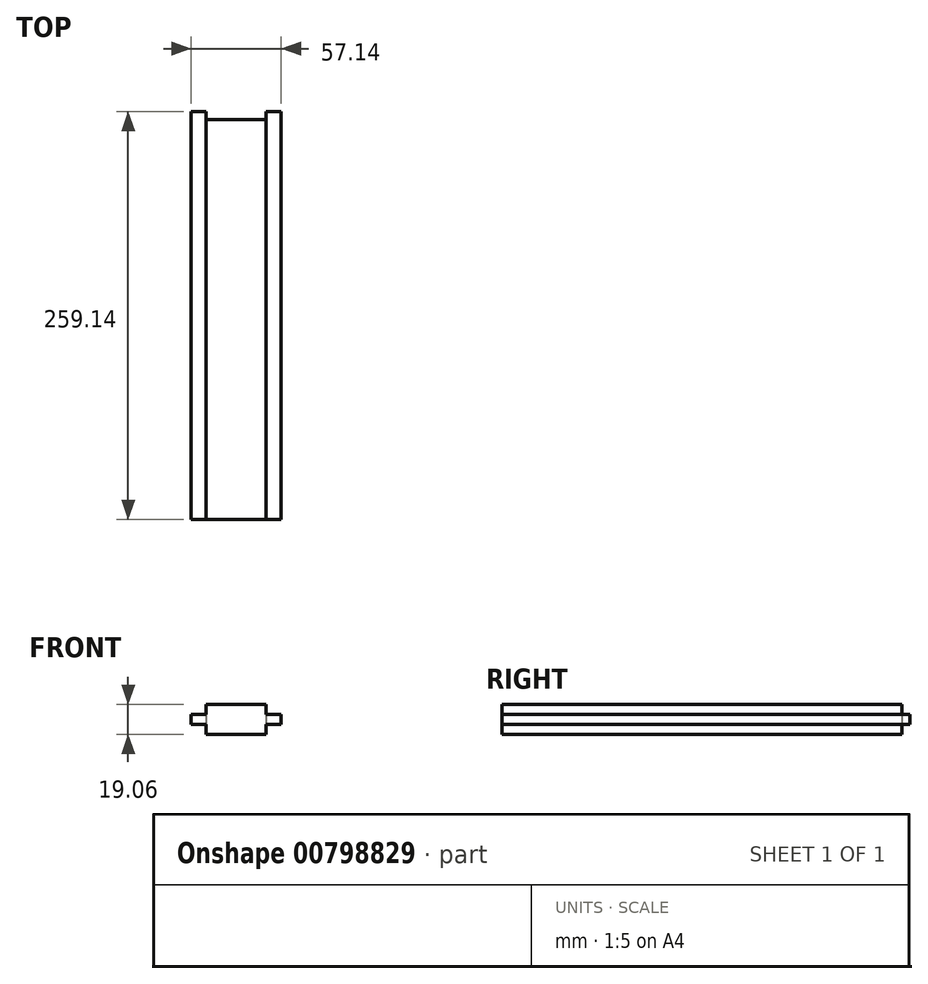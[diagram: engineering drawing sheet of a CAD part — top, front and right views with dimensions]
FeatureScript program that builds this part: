
annotation { "Feature Type Name" : "Feature", "Feature Type Description" : "" }
export const myFeature = defineFeature(function(context is Context, id is Id, definition is map)
    precondition{}
    {
        {
            var Q0;
            Q0=qCreatedBy(makeId("Front.planeOp"),FACE);
            var sketch = newSketch(context, id + "F0", { "sketchPlane" : qUnion([Q0])});
            skLineSegment(sketch, "E0.bottom", {"start": v(-19.05, 9.52) * mm, "end": v(19.05, 9.52) * mm});
            skLineSegment(sketch, "E0.top", {"start": v(-19.05, -9.53) * mm, "end": v(19.05, -9.53) * mm});
            skLineSegment(sketch, "E0.left", {"start": v(-19.05, 9.52) * mm, "end": v(-19.05, -9.53) * mm});
            skLineSegment(sketch, "E0.right", {"start": v(19.05, 9.53) * mm, "end": v(19.05, -9.52) * mm});
            skSolve(sketch);
        }
        {
            var Q0;
            Q0=makeQuery(id+"F0.imprint","IMPRINT",FACE,{"disambiguationData":[TD([[makeQuery(id+"F0.imprint","IMPRINT",EDGE,{"derivedFrom":sQuery(id+"F0.wireOp",EDGE,"E0.bottom")}),-1.0]])]});
            extrude(context, id + "F1", {"entities" : qUnion([Q0]), "depth" : 254 * mm, "offsetDistance" : 25.4 * mm});
        }
        {
            var Q0;
            Q0=makeQuery(id+"F1.opExtrude","CAP_FACE",FACE,{"disambiguationData":[OSD([sQuery(id+"F0.wireOp",EDGE,"E0.bottom"),sQuery(id+"F0.wireOp",EDGE,"E0.top"),sQuery(id+"F0.wireOp",EDGE,"E0.left"),sQuery(id+"F0.wireOp",EDGE,"E0.right")])],"isStart":false});
            var sketch = newSketch(context, id + "F2", { "sketchPlane" : qUnion([Q0])});
            skLineSegment(sketch, "E1.bottom", {"start": v(-19.05, 3.17) * mm, "end": v(-28.58, 3.17) * mm});
            skLineSegment(sketch, "E1.top", {"start": v(-19.05, -3.05) * mm, "end": v(-28.58, -3.05) * mm});
            skLineSegment(sketch, "E1.left", {"start": v(-19.05, 3.17) * mm, "end": v(-19.05, -3.05) * mm});
            skLineSegment(sketch, "E1.right", {"start": v(-28.58, 3.17) * mm, "end": v(-28.58, -3.05) * mm});
            skSolve(sketch);
        }
        {
            var Q0;
            Q0=qSketchRegion(id+"F2",true);
            extrude(context, id + "F3", {"entities" : qUnion([Q0]), "endBound" : BoundingType.THROUGH_ALL, "oppositeDirection" : true, "depth" : 25.4 * mm, "offsetDistance" : 25.4 * mm});
        }
        {
            var Q0;
            Q0=makeQuery(id+"F3.opExtrude","SWEPT_BODY",BODY,{"disambiguationData":[OSD([sQuery(id+"F2.wireOp",EDGE,"E1.bottom"),sQuery(id+"F2.wireOp",EDGE,"E1.top"),sQuery(id+"F2.wireOp",EDGE,"E1.left"),sQuery(id+"F2.wireOp",EDGE,"E1.right")])]});
            var Q1;
            Q1=qCreatedBy(makeId("Right.planeOp"),FACE);
            mirror(context, id + "F4", {"operationType" : NewBodyOperationType.ADD, "entities" : qUnion([Q0]), "mirrorPlane" : qUnion([Q1])});
        }
    });
